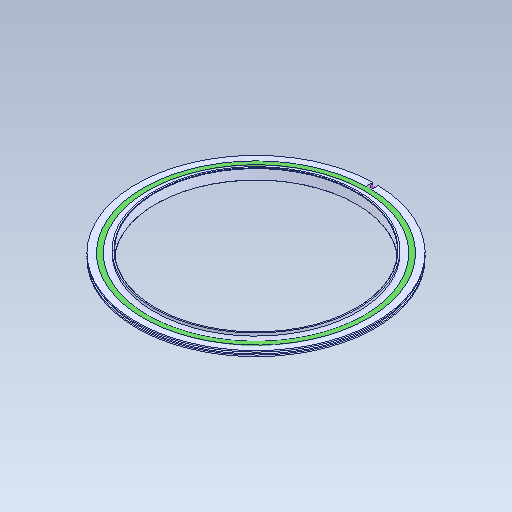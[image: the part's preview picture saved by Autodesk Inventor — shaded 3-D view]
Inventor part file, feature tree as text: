
AUTODESK INVENTOR PART (.ipt)
format: ipt  version: 2021 (Build 250183000, 183)  size: 233,472 bytes
history: native  units: in
note: dims shown in document units (in); Inventor stores cm internally (conversion verified against a paired STEP export)
features: revolve x2, chamfer x1, other x1
ambient origin geometry x8: Origin, YZ Plane, XZ Plane, XY Plane, X Axis, Y Axis, Z Axis, Center Point
bodies: Solid1 (feature_tree), Solid2 (feature_tree), Solid3 (feature_tree), Solid4 (feature_tree)
feature tree (4):
  chamfer  "Chamfer1"  [1 undecoded]
  revolve  "Revolve2"  [1 undecoded]
  other  "Cut-Extrude1"
  revolve  "Revolve4"  [1 undecoded]
note: 3 required parameter values undecoded (feature->parameter linkage not recoverable at this tier; creation-order binding heuristic only, values carry confidence <= 0.55)
